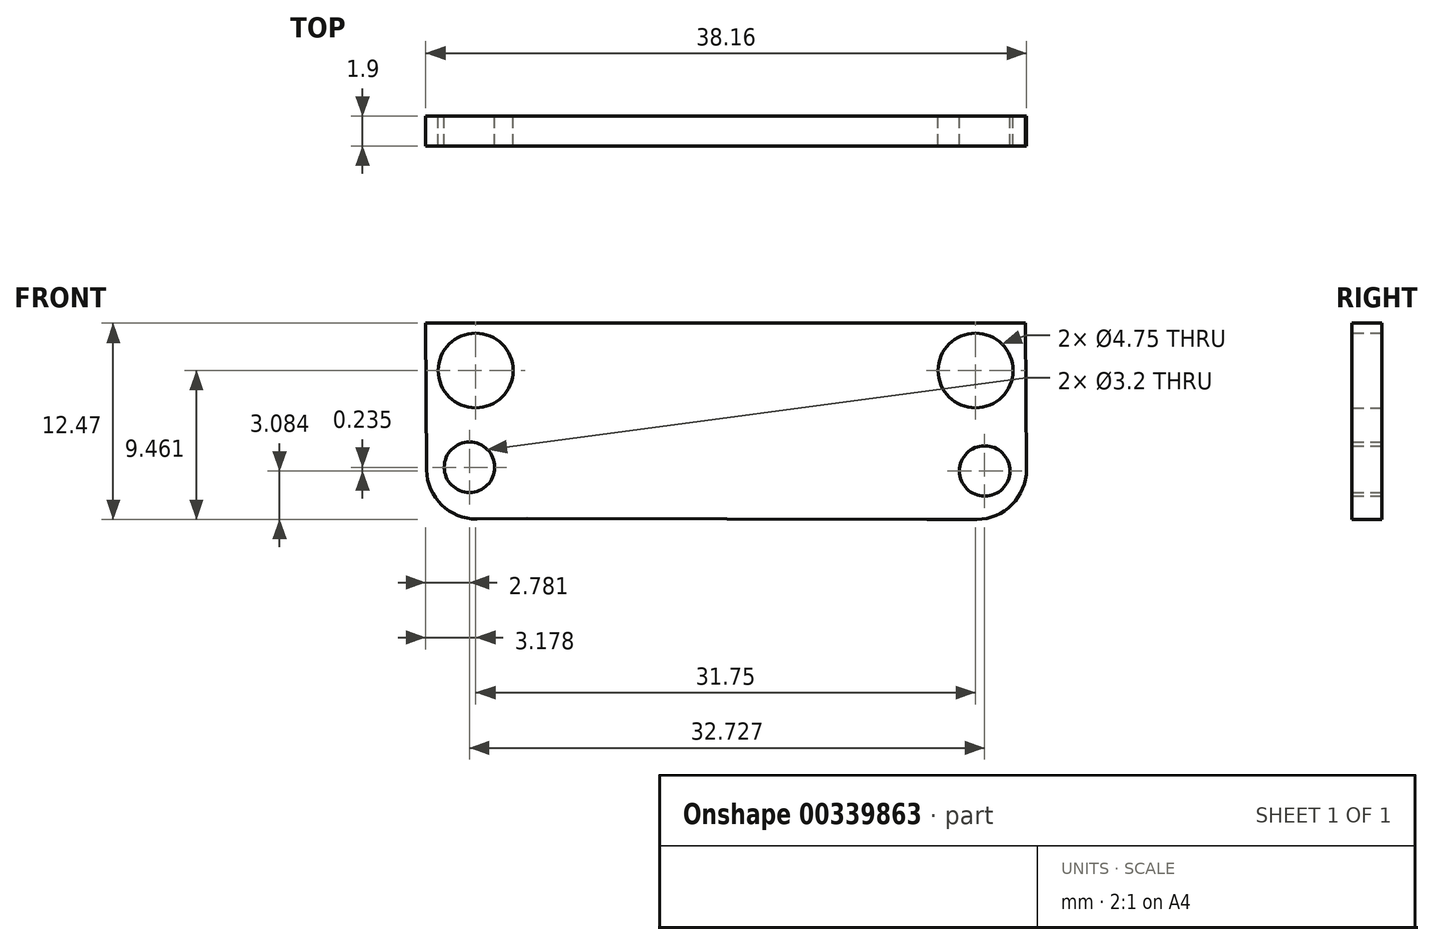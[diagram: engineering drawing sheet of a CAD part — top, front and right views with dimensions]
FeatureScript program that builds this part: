
annotation { "Feature Type Name" : "Feature", "Feature Type Description" : "" }
export const myFeature = defineFeature(function(context is Context, id is Id, definition is map)
    precondition{}
    {
        {
            var Q0;
            Q0=qCreatedBy(makeId("Front.planeOp"),FACE);
            var sketch = newSketch(context, id + "F0", { "sketchPlane" : qUnion([Q0])});
            skLineSegment(sketch, "E0.bottom", {"start": v(-7.3, 27.75) * mm, "end": v(30.8, 27.75) * mm});
            skLineSegment(sketch, "E0.left", {"start": v(-7.3, 27.75) * mm, "end": v(-7.24, 18.2) * mm});
            skLineSegment(sketch, "E0.right", {"start": v(30.8, 27.75) * mm, "end": v(30.86, 18.47) * mm});
            skCircle(sketch, "E1", {"center": v(27.63, 24.74) * mm, "radius": 2.37 * mm});
            skCircle(sketch, "E2.MirrorC", {"center": v(-4.12, 24.74) * mm, "radius": 2.37 * mm});
            skCircle(sketch, "E3", {"center": v(28.2, 18.36) * mm, "radius": 1.6 * mm});
            skCircle(sketch, "E4.MirrorC", {"center": v(-4.52, 18.6) * mm, "radius": 1.6 * mm});
            skPoint(sketch, "E5.visualSharp", {"position": v(30.88, 15.28) * mm});
            skArc(sketch, "E5.filletArc", {"start": v(27.7, 15.28) * mm, "mid": v(29.94, 16.22) * mm, "end": v(30.86, 18.47) * mm});
            skLineSegment(sketch, "E6", {"start": v(24.53, 15.28) * mm, "end": v(27.7, 15.28) * mm});
            skLineSegment(sketch, "E7", {"start": v(-0.87, 15.33) * mm, "end": v(-4.05, 15.31) * mm});
            skLineSegment(sketch, "E8", {"start": v(-7.24, 18.2) * mm, "end": v(-7.24, 18.46) * mm});
            skPoint(sketch, "E9.visualSharp", {"position": v(-7.22, 15.3) * mm});
            skArc(sketch, "E9.filletArc", {"start": v(-7.24, 18.46) * mm, "mid": v(-6.3, 16.23) * mm, "end": v(-4.05, 15.31) * mm});
            skLineSegment(sketch, "E10", {"start": v(-0.87, 15.33) * mm, "end": v(24.53, 15.28) * mm});
            skSolve(sketch);
        }
        {
            var Q0;
            Q0=makeQuery(id+"F0.imprint","IMPRINT",FACE,{"disambiguationData":[TD([[makeQuery(id+"F0.imprint","IMPRINT",EDGE,{"derivedFrom":sQuery(id+"F0.wireOp",EDGE,"E0.bottom")}),-1.0]])]});
            extrude(context, id + "F1", {"entities" : qUnion([Q0]), "depth" : 1.9 * mm});
        }
    });
